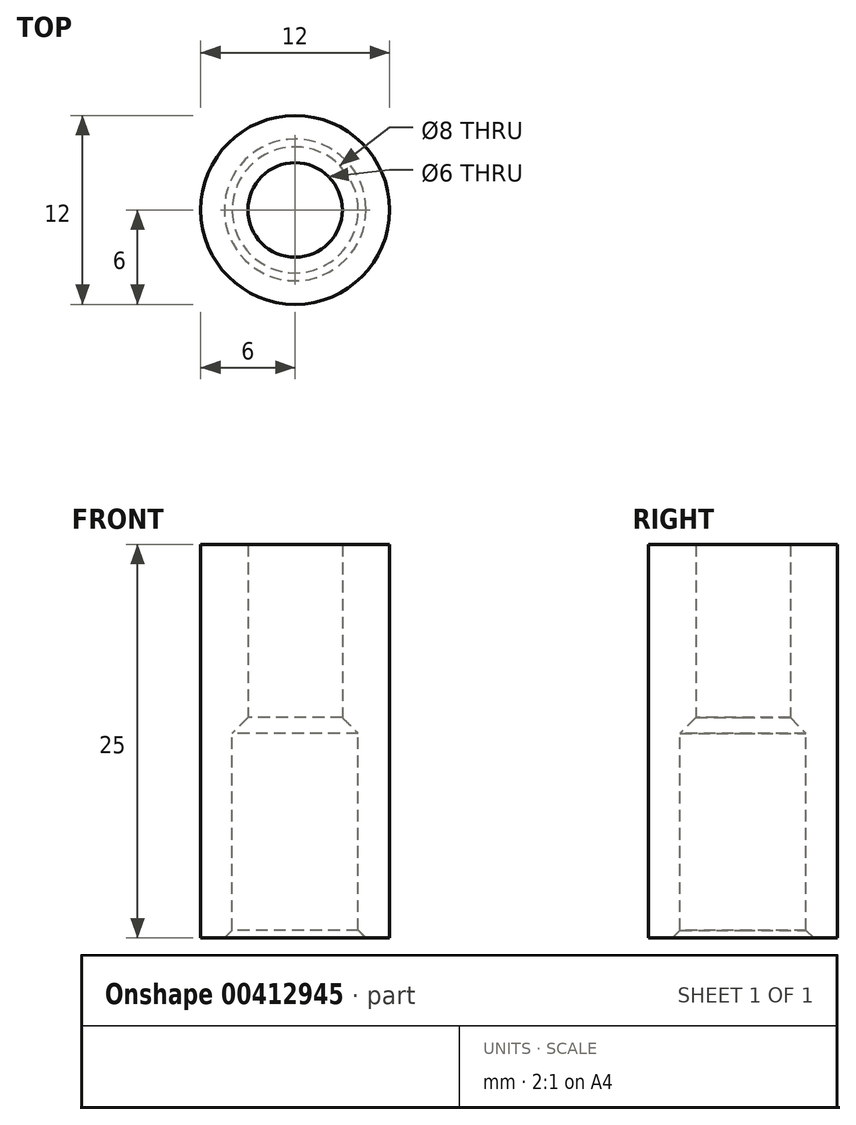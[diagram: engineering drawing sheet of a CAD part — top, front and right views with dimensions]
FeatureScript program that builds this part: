
annotation { "Feature Type Name" : "Feature", "Feature Type Description" : "" }
export const myFeature = defineFeature(function(context is Context, id is Id, definition is map)
    precondition{}
    {
        {
            var Q0;
            Q0=qCreatedBy(makeId("Top.planeOp"),FACE);
            var sketch = newSketch(context, id + "F0", { "sketchPlane" : qUnion([Q0])});
            skCircle(sketch, "E0", {"center": v(0, 0) * mm, "radius": 4 * mm});
            skCircle(sketch, "E1", {"center": v(0, 0) * mm, "radius": 3 * mm});
            skCircle(sketch, "E2", {"center": v(0, 0) * mm, "radius": 6 * mm});
            skSolve(sketch);
        }
        {
            var Q0;
            Q0 = qSketchRegion(id + "F0", true);
            extrude(context, id + "F1", {"entities" : qUnion([Q0]), "oppositeDirection" : true, "depth" : 13 * mm, "offsetDistance" : 25 * mm});
        }
        {
            var Q0;
            Q0=makeQuery(id+"F0.imprint","IMPRINT",FACE,{"disambiguationData":[TD([[makeQuery(id+"F0.imprint","IMPRINT",EDGE,{"derivedFrom":sQuery(id+"F0.wireOp",EDGE,"E0")}),-1.0]])]});
            var Q1;
            Q1=makeQuery(id+"F0.imprint","IMPRINT",FACE,{"disambiguationData":[TD([[makeQuery(id+"F0.imprint","IMPRINT",EDGE,{"derivedFrom":sQuery(id+"F0.wireOp",EDGE,"E0")}),1.0]])]});
            extrude(context, id + "F2", {"entities" : qUnion([Q0, Q1]), "operationType" : NewBodyOperationType.ADD, "depth" : 12 * mm, "offsetDistance" : 25 * mm});
        }
        {
            var Q0;
            Q0=makeQuery(id+"F2.opExtrude","CAP_EDGE",EDGE,{"disambiguationData":[OSD([sQuery(id+"F0.wireOp",EDGE,"E1")])],"isStart":true});
            chamfer(context, id + "F3", {"entities" : qUnion([Q0]), "width" : 1 * mm, "tangentPropagation" : true});
        }
        {
            var Q0;
            Q0=makeQuery(id+"F1.opExtrude","CAP_EDGE",EDGE,{"disambiguationData":[OSD([sQuery(id+"F0.wireOp",EDGE,"E0")])],"isStart":false});
            chamfer(context, id + "F4", {"entities" : qUnion([Q0]), "width" : 0.5 * mm, "tangentPropagation" : true});
        }
    });
